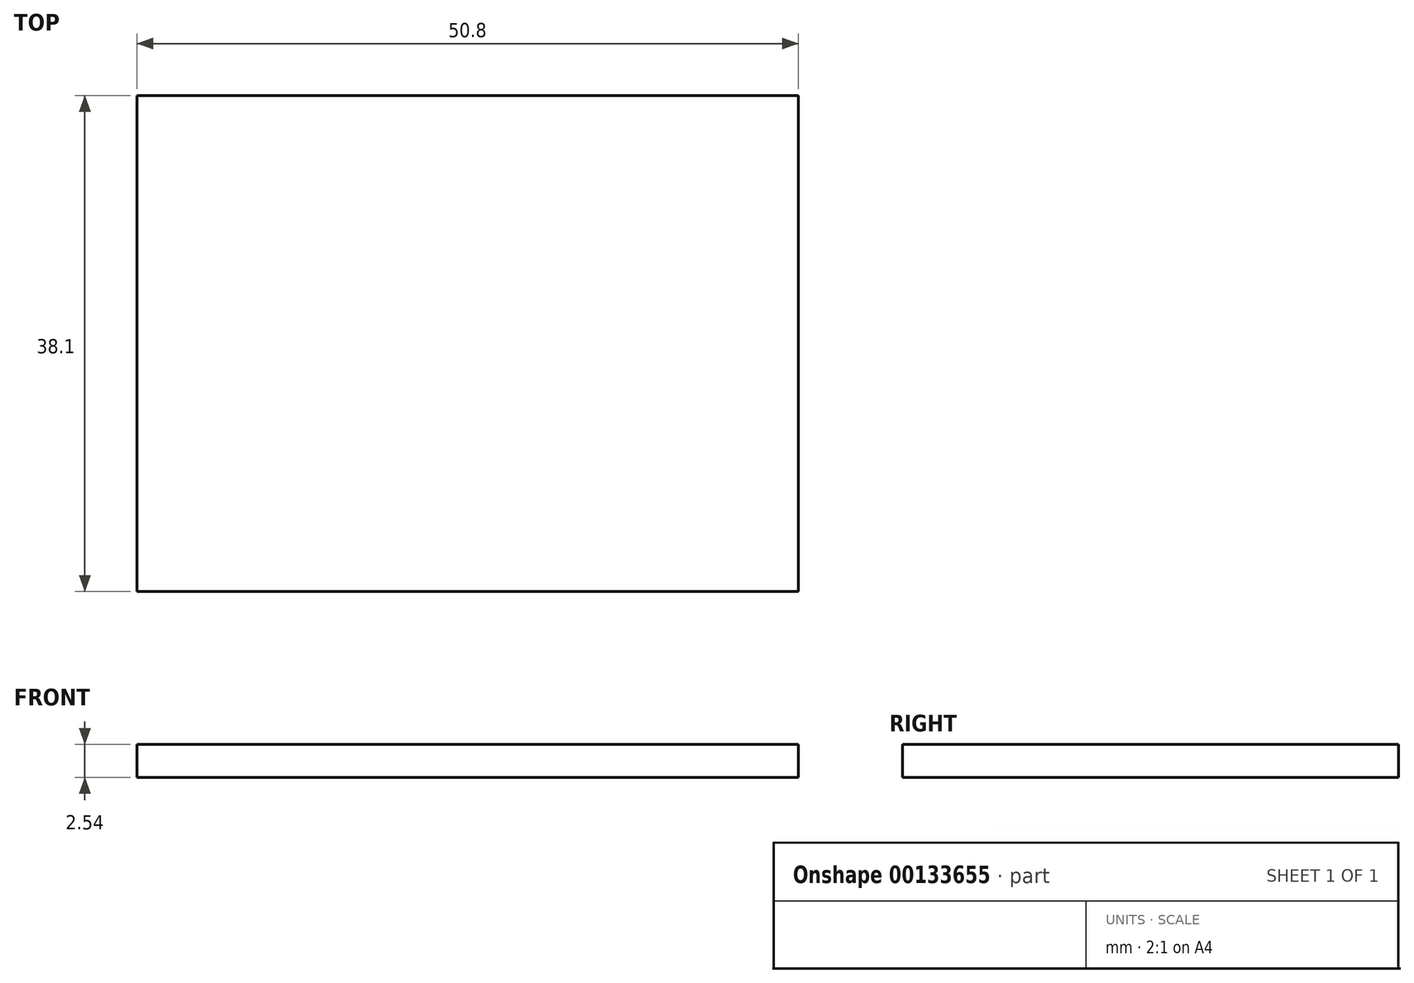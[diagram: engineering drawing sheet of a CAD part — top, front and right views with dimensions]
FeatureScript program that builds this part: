
annotation { "Feature Type Name" : "Feature", "Feature Type Description" : "" }
export const myFeature = defineFeature(function(context is Context, id is Id, definition is map)
    precondition{}
    {
        {
            var Q0;
            Q0=qCreatedBy(makeId("Top.planeOp"),FACE);
            var sketch = newSketch(context, id + "F0", { "sketchPlane" : qUnion([Q0])});
            skLineSegment(sketch, "E0.bottom", {"start": v(0, 38.1) * mm, "end": v(50.8, 38.1) * mm});
            skLineSegment(sketch, "E0.top", {"start": v(0, 0) * mm, "end": v(50.8, 0) * mm});
            skLineSegment(sketch, "E0.left", {"start": v(50.8, 38.1) * mm, "end": v(50.8, 0) * mm});
            skLineSegment(sketch, "E0.right", {"start": v(0, 38.1) * mm, "end": v(0, 0) * mm});
            skSolve(sketch);
        }
        {
            var Q0;
            Q0=makeQuery(id+"F0.imprint","IMPRINT",FACE,{"disambiguationData":[TD([[makeQuery(id+"F0.imprint","IMPRINT",EDGE,{"derivedFrom":sQuery(id+"F0.wireOp",EDGE,"E0.bottom")}),-1.0]])]});
            extrude(context, id + "F1", {"entities" : qUnion([Q0]), "depth" : 2.54 * mm});
        }
        {
            var Q0;
            Q0=qCreatedBy(makeId("Top.planeOp"),FACE);
            cPlane(context, id + "F2", {"entities" : qUnion([Q0]), "cplaneType" : CPlaneType.OFFSET, "offset" : 25.4 * mm, "width" : 152.4 * mm, "height" : 152.4 * mm});
        }
        {
            var Q0;
            Q0=qCreatedBy(id+"F2.planeOp",FACE);
            var sketch = newSketch(context, id + "F3", { "sketchPlane" : qUnion([Q0])});
            skArc(sketch, "E1", {"start": v(33.02, 12.7) * mm, "mid": v(31.75, 13.97) * mm, "end": v(30.48, 12.7) * mm});
            skLineSegment(sketch, "E2", {"start": v(33.57, 12.7) * mm, "end": v(29.91, 12.7) * mm, "construction": true});
            skPoint(sketch, "E3", {"position": v(30.48, 12.7) * mm});
            skPoint(sketch, "E4", {"position": v(33.02, 12.7) * mm});
            skSolve(sketch);
        }
        {
            var Q0;
            Q0=sQuery(id+"F3.wireOp",EDGE,"E1");
            var Q1;
            Q1=sQuery(id+"F3.wireOp",EDGE,"E2");
            revolve(context, id + "F4", {"bodyType" : ToolBodyType.SURFACE, "surfaceEntities" : qUnion([Q0]), "axis" : qUnion([Q1]), "revolveType" : RevolveType.FULL});
        }
    });
